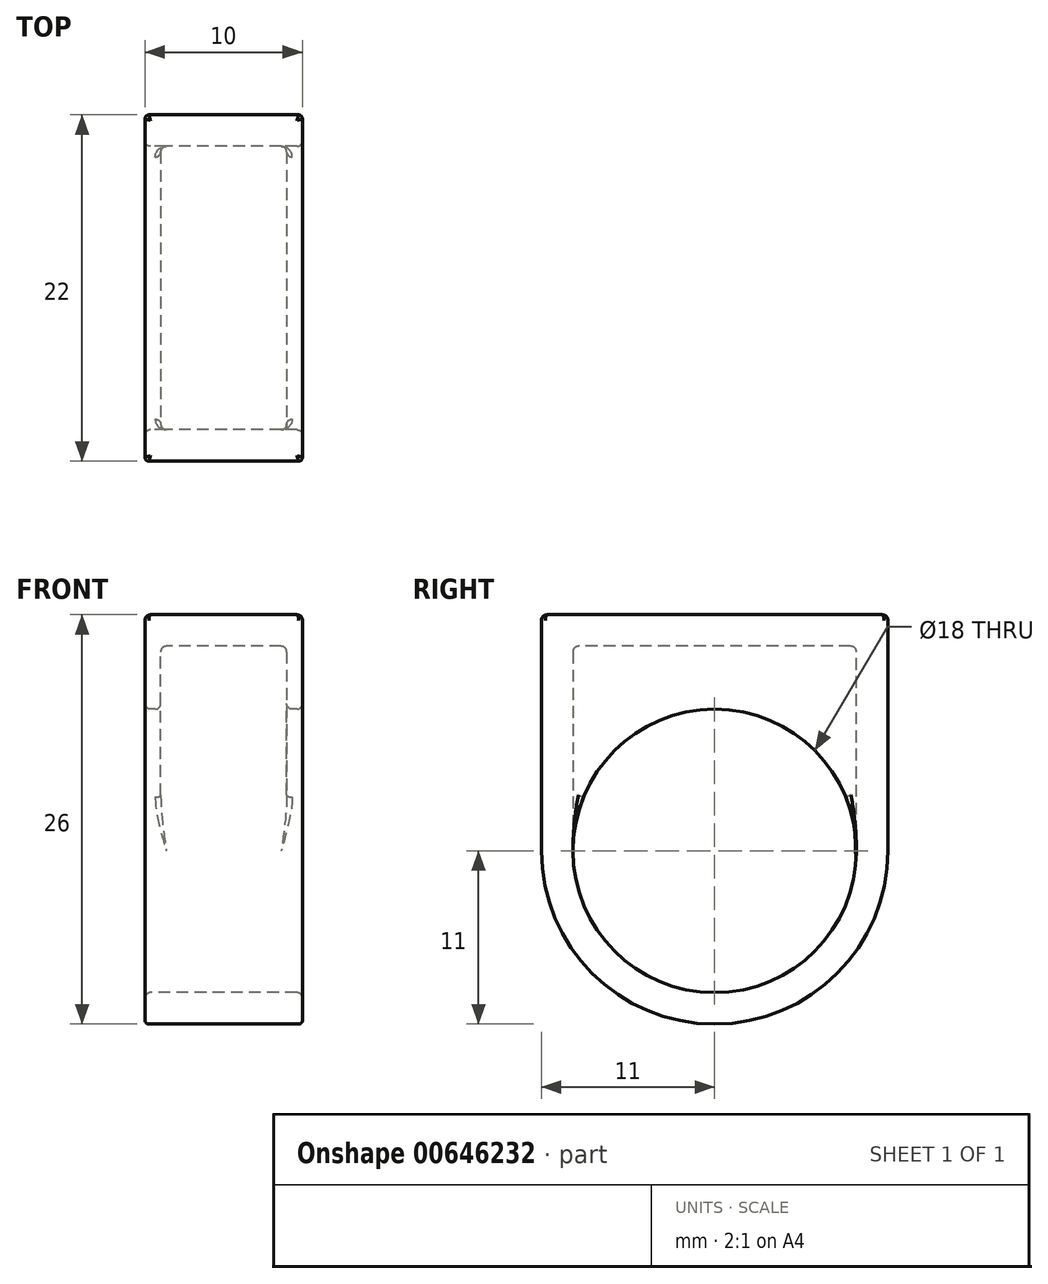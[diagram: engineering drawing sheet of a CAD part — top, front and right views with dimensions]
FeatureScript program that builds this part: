
annotation { "Feature Type Name" : "Feature", "Feature Type Description" : "" }
export const myFeature = defineFeature(function(context is Context, id is Id, definition is map)
    precondition{}
    {
        {
            var Q0;
            Q0=qCreatedBy(makeId("Right.planeOp"),FACE);
            var sketch = newSketch(context, id + "F0", { "sketchPlane" : qUnion([Q0])});
            skCircle(sketch, "E0", {"center": v(0, 0) * mm, "radius": 9 * mm});
            skArc(sketch, "E1", {"start": v(-11, 0) * mm, "mid": v(0, -11) * mm, "end": v(11, 0) * mm});
            skLineSegment(sketch, "E2", {"start": v(-11, 0) * mm, "end": v(-11, 15) * mm});
            skLineSegment(sketch, "E3", {"start": v(11, 0) * mm, "end": v(11, 15) * mm});
            skLineSegment(sketch, "E4", {"start": v(11, 15) * mm, "end": v(-11, 15) * mm});
            skSolve(sketch);
        }
        {
            var Q0;
            Q0=makeQuery(id+"F0.imprint","IMPRINT",FACE,{"disambiguationData":[TD([[makeQuery(id+"F0.imprint","IMPRINT",EDGE,{"derivedFrom":sQuery(id+"F0.wireOp",EDGE,"E0")}),-1.0]])]});
            extrude(context, id + "F1", {"entities" : qUnion([Q0]), "endBound" : BoundingType.SYMMETRIC, "depth" : 10 * mm, "offsetDistance" : 25 * mm});
        }
        {
            var Q0;
            Q0=qCreatedBy(makeId("Right.planeOp"),FACE);
            var sketch = newSketch(context, id + "F2", { "sketchPlane" : qUnion([Q0])});
            skLineSegment(sketch, "E5.0", {"start": v(9, 0) * mm, "end": v(9, 13) * mm});
            skArc(sketch, "E5.1", {"start": v(-9, 0) * mm, "mid": v(0, -9) * mm, "end": v(9, 0) * mm});
            skLineSegment(sketch, "E5.2", {"start": v(-9, 13) * mm, "end": v(-9, 0) * mm});
            skLineSegment(sketch, "E5.3", {"start": v(9, 13) * mm, "end": v(-9, 13) * mm});
            skSolve(sketch);
        }
        {
            var Q0;
            Q0 = qSketchRegion(id + "F2", true);
            extrude(context, id + "F3", {"entities" : qUnion([Q0]), "operationType" : NewBodyOperationType.REMOVE, "endBound" : BoundingType.SYMMETRIC, "depth" : 8 * mm, "offsetDistance" : 25 * mm});
        }
        {
            var Q0;
            Q0=makeQuery(id+"F1.opExtrude","CAP_EDGE",EDGE,{"disambiguationData":[OSD([sQuery(id+"F0.wireOp",EDGE,"E2")])],"isStart":true});
            var Q1;
            Q1=makeQuery(id+"F1.opExtrude","CAP_EDGE",EDGE,{"disambiguationData":[OSD([sQuery(id+"F0.wireOp",EDGE,"E2")])],"isStart":false});
            fillet(context, id + "F4", {"entities" : qUnion([Q0, Q1]), "radius" : 0.25 * mm, "tangentPropagation" : true, "allowEdgeOverflow" : false});
        }
        {
            var Q0;
            Q0=makeQuery(id+"F1.opExtrude","CAP_EDGE",EDGE,{"disambiguationData":[OSD([sQuery(id+"F0.wireOp",EDGE,"E0")])],"isStart":true});
            var Q1;
            {var subQ0=sQuery(id+"F0.wireOp",EDGE,"E2");Q1=makeQuery(id+"F4.opFillet","BLEND_FACE",FACE,{"disambiguationData":[OSD([subQ0]),TDD([makeQuery(id+"F1.opExtrude","CAP_EDGE",EDGE,{"disambiguationData":[OSD([subQ0])],"isStart":true})])]});}
            var Q2;
            Q2=makeQuery(id+"F1.opExtrude","SWEPT_EDGE",EDGE,{"disambiguationData":[OSD([sQuery(id+"F0.wireOp",EDGE,"E3"),sQuery(id+"F0.wireOp",EDGE,"E4")])]});
            var Q3;
            {var subQ0=sQuery(id+"F0.wireOp",EDGE,"E2");Q3=makeQuery(id+"F4.opFillet","BLEND_FACE",FACE,{"disambiguationData":[OSD([subQ0]),TDD([makeQuery(id+"F1.opExtrude","CAP_EDGE",EDGE,{"disambiguationData":[OSD([subQ0])],"isStart":false})])]});}
            var Q4;
            Q4=makeQuery(id+"F1.opExtrude","SWEPT_EDGE",EDGE,{"disambiguationData":[OSD([sQuery(id+"F0.wireOp",EDGE,"E2"),sQuery(id+"F0.wireOp",EDGE,"E4")])]});
            var Q5;
            {var subQ0=sQuery(id+"F0.wireOp",EDGE,"E3");Q5=makeQuery(id+"F4.opFillet","BLEND_FACE",FACE,{"disambiguationData":[OSD([subQ0]),TDD([makeQuery(id+"F1.opExtrude","CAP_EDGE",EDGE,{"disambiguationData":[OSD([subQ0])],"isStart":false})])]});}
            var Q6;
            {var subQ0=sQuery(id+"F0.wireOp",EDGE,"E1");Q6=makeQuery(id+"F4.opFillet","BLEND_FACE",FACE,{"disambiguationData":[OSD([subQ0]),TDD([makeQuery(id+"F1.opExtrude","CAP_EDGE",EDGE,{"disambiguationData":[OSD([subQ0])],"isStart":false})])]});}
            var Q7;
            Q7=makeQuery(id+"F1.opExtrude","CAP_EDGE",EDGE,{"disambiguationData":[OSD([sQuery(id+"F0.wireOp",EDGE,"E0")])],"isStart":false});
            var Q8;
            {var subQ0=sQuery(id+"F0.wireOp",EDGE,"E1");Q8=makeQuery(id+"F4.opFillet","BLEND_FACE",FACE,{"disambiguationData":[OSD([subQ0]),TDD([makeQuery(id+"F1.opExtrude","CAP_EDGE",EDGE,{"disambiguationData":[OSD([subQ0])],"isStart":true})])]});}
            var Q9;
            Q9=makeQuery(id+"F1.opExtrude","SWEPT_EDGE",EDGE,{"disambiguationData":[OSD([sQuery(id+"F0.wireOp",EDGE,"E1"),sQuery(id+"F0.wireOp",EDGE,"E2")])]});
            var Q10;
            Q10=makeQuery(id+"F3.boolean.opBoolean","INTERSECT",EDGE,{"derivedFrom":[makeQuery(id+"F1.opExtrude","SWEPT_FACE",FACE,{"disambiguationData":[OSD([sQuery(id+"F0.wireOp",EDGE,"E0")])]}),makeQuery(id+"F3.opExtrude","CAP_FACE",FACE,{"disambiguationData":[OSD([sQuery(id+"F2.wireOp",EDGE,"E5.0"),sQuery(id+"F2.wireOp",EDGE,"E5.1"),sQuery(id+"F2.wireOp",EDGE,"E5.2"),sQuery(id+"F2.wireOp",EDGE,"E5.3")])],"isStart":false})]});
            var Q11;
            Q11=makeQuery(id+"F1.opExtrude","SWEPT_FACE",FACE,{"disambiguationData":[OSD([sQuery(id+"F0.wireOp",EDGE,"E0")])]});
            var Q12;
            Q12=makeQuery(id+"F3.boolean.opBoolean","COPY",FACE,{"derivedFrom":makeQuery(id+"F3.opExtrude","CAP_FACE",FACE,{"disambiguationData":[OSD([sQuery(id+"F2.wireOp",EDGE,"E5.0"),sQuery(id+"F2.wireOp",EDGE,"E5.1"),sQuery(id+"F2.wireOp",EDGE,"E5.2"),sQuery(id+"F2.wireOp",EDGE,"E5.3")])],"isStart":false})});
            var Q13;
            Q13=makeQuery(id+"F3.boolean.opBoolean","COPY",FACE,{"derivedFrom":makeQuery(id+"F3.opExtrude","SWEPT_FACE",FACE,{"disambiguationData":[OSD([sQuery(id+"F2.wireOp",EDGE,"E5.0")])]})});
            var Q14;
            Q14=makeQuery(id+"F3.boolean.opBoolean","COPY",EDGE,{"derivedFrom":makeQuery(id+"F3.opExtrude","SWEPT_EDGE",EDGE,{"disambiguationData":[OSD([sQuery(id+"F2.wireOp",EDGE,"E5.0"),sQuery(id+"F2.wireOp",EDGE,"E5.1")])]})});
            var Q15;
            Q15=makeQuery(id+"F1.opExtrude","CAP_FACE",FACE,{"disambiguationData":[OSD([sQuery(id+"F0.wireOp",EDGE,"E0"),sQuery(id+"F0.wireOp",EDGE,"E1"),sQuery(id+"F0.wireOp",EDGE,"E2"),sQuery(id+"F0.wireOp",EDGE,"E3"),sQuery(id+"F0.wireOp",EDGE,"E4")])],"isStart":true});
            var Q16;
            {var subQ0=sQuery(id+"F0.wireOp",EDGE,"E1");Q16=makeQuery(id+"F4.opFillet","BLEND_EDGE",EDGE,{"blendedFrom":[makeQuery(id+"F1.opExtrude","CAP_EDGE",EDGE,{"disambiguationData":[OSD([subQ0])],"isStart":true}),makeQuery(id+"F1.opExtrude","SWEPT_FACE",FACE,{"disambiguationData":[OSD([subQ0])]})],"blendedInto":[makeQuery(id+"F1.opExtrude","SWEPT_FACE",FACE,{"disambiguationData":[OSD([subQ0])]})]});}
            var Q17;
            Q17=makeQuery(id+"F1.opExtrude","CAP_FACE",FACE,{"disambiguationData":[OSD([sQuery(id+"F0.wireOp",EDGE,"E0"),sQuery(id+"F0.wireOp",EDGE,"E1"),sQuery(id+"F0.wireOp",EDGE,"E2"),sQuery(id+"F0.wireOp",EDGE,"E3"),sQuery(id+"F0.wireOp",EDGE,"E4")])],"isStart":false});
            var Q18;
            Q18=makeQuery(id+"F1.opExtrude","SWEPT_FACE",FACE,{"disambiguationData":[OSD([sQuery(id+"F0.wireOp",EDGE,"E1")])]});
            var Q19;
            Q19=makeQuery(id+"F1.opExtrude","SWEPT_FACE",FACE,{"disambiguationData":[OSD([sQuery(id+"F0.wireOp",EDGE,"E2")])]});
            var Q20;
            {var subQ0=sQuery(id+"F0.wireOp",EDGE,"E1");Q20=makeQuery(id+"F4.opFillet","BLEND_EDGE",EDGE,{"blendedFrom":[makeQuery(id+"F1.opExtrude","CAP_EDGE",EDGE,{"disambiguationData":[OSD([subQ0])],"isStart":false}),makeQuery(id+"F1.opExtrude","CAP_FACE",FACE,{"disambiguationData":[OSD([sQuery(id+"F0.wireOp",EDGE,"E0"),subQ0,sQuery(id+"F0.wireOp",EDGE,"E2"),sQuery(id+"F0.wireOp",EDGE,"E3"),sQuery(id+"F0.wireOp",EDGE,"E4")])],"isStart":false})],"blendedInto":[makeQuery(id+"F1.opExtrude","CAP_FACE",FACE,{"disambiguationData":[OSD([sQuery(id+"F0.wireOp",EDGE,"E0"),subQ0,sQuery(id+"F0.wireOp",EDGE,"E2"),sQuery(id+"F0.wireOp",EDGE,"E3"),sQuery(id+"F0.wireOp",EDGE,"E4")])],"isStart":false})]});}
            var Q21;
            Q21=makeQuery(id+"F1.opExtrude","SWEPT_FACE",FACE,{"disambiguationData":[OSD([sQuery(id+"F0.wireOp",EDGE,"E3")])]});
            var Q22;
            {var subQ0=sQuery(id+"F0.wireOp",EDGE,"E1");Q22=makeQuery(id+"F4.opFillet","BLEND_EDGE",EDGE,{"blendedFrom":[makeQuery(id+"F1.opExtrude","CAP_EDGE",EDGE,{"disambiguationData":[OSD([subQ0])],"isStart":false}),makeQuery(id+"F1.opExtrude","SWEPT_FACE",FACE,{"disambiguationData":[OSD([subQ0])]})],"blendedInto":[makeQuery(id+"F1.opExtrude","SWEPT_FACE",FACE,{"disambiguationData":[OSD([subQ0])]})]});}
            var Q23;
            Q23=makeQuery(id+"F1.opExtrude","SWEPT_FACE",FACE,{"disambiguationData":[OSD([sQuery(id+"F0.wireOp",EDGE,"E4")])]});
            var Q24;
            Q24=makeQuery(id+"F4.opFillet","BLEND_EDGE",EDGE,{"blendedFrom":[makeQuery(id+"F1.opExtrude","CAP_EDGE",EDGE,{"disambiguationData":[OSD([sQuery(id+"F0.wireOp",EDGE,"E2")])],"isStart":false}),makeQuery(id+"F1.opExtrude","SWEPT_FACE",FACE,{"disambiguationData":[OSD([sQuery(id+"F0.wireOp",EDGE,"E4")])]})],"blendedInto":[makeQuery(id+"F1.opExtrude","SWEPT_FACE",FACE,{"disambiguationData":[OSD([sQuery(id+"F0.wireOp",EDGE,"E4")])]})]});
            var Q25;
            Q25=makeQuery(id+"F1.opExtrude","CAP_EDGE",EDGE,{"disambiguationData":[OSD([sQuery(id+"F0.wireOp",EDGE,"E4")])],"isStart":true});
            var Q26;
            Q26=makeQuery(id+"F1.opExtrude","CAP_EDGE",EDGE,{"disambiguationData":[OSD([sQuery(id+"F0.wireOp",EDGE,"E4")])],"isStart":false});
            var Q27;
            {var subQ0=sQuery(id+"F0.wireOp",EDGE,"E3");Q27=makeQuery(id+"F4.opFillet","BLEND_FACE",FACE,{"disambiguationData":[OSD([subQ0]),TDD([makeQuery(id+"F1.opExtrude","CAP_EDGE",EDGE,{"disambiguationData":[OSD([subQ0])],"isStart":true})])]});}
            var Q28;
            Q28=makeQuery(id+"F3.boolean.opBoolean","COPY",FACE,{"derivedFrom":makeQuery(id+"F3.opExtrude","CAP_FACE",FACE,{"disambiguationData":[OSD([sQuery(id+"F2.wireOp",EDGE,"E5.0"),sQuery(id+"F2.wireOp",EDGE,"E5.1"),sQuery(id+"F2.wireOp",EDGE,"E5.2"),sQuery(id+"F2.wireOp",EDGE,"E5.3")])],"isStart":true})});
            var Q29;
            {var subQ0=sQuery(id+"F0.wireOp",EDGE,"E1");Q29=makeQuery(id+"F4.opFillet","BLEND_EDGE",EDGE,{"blendedFrom":[makeQuery(id+"F1.opExtrude","CAP_EDGE",EDGE,{"disambiguationData":[OSD([subQ0])],"isStart":true}),makeQuery(id+"F1.opExtrude","CAP_FACE",FACE,{"disambiguationData":[OSD([sQuery(id+"F0.wireOp",EDGE,"E0"),subQ0,sQuery(id+"F0.wireOp",EDGE,"E2"),sQuery(id+"F0.wireOp",EDGE,"E3"),sQuery(id+"F0.wireOp",EDGE,"E4")])],"isStart":true})],"blendedInto":[makeQuery(id+"F1.opExtrude","CAP_FACE",FACE,{"disambiguationData":[OSD([sQuery(id+"F0.wireOp",EDGE,"E0"),subQ0,sQuery(id+"F0.wireOp",EDGE,"E2"),sQuery(id+"F0.wireOp",EDGE,"E3"),sQuery(id+"F0.wireOp",EDGE,"E4")])],"isStart":true})]});}
            var Q30;
            Q30=makeQuery(id+"F3.boolean.opBoolean","COPY",EDGE,{"derivedFrom":makeQuery(id+"F3.opExtrude","CAP_EDGE",EDGE,{"disambiguationData":[OSD([sQuery(id+"F2.wireOp",EDGE,"E5.0")])],"isStart":true})});
            var Q31;
            Q31=makeQuery(id+"F1.opExtrude","SWEPT_EDGE",EDGE,{"disambiguationData":[OSD([sQuery(id+"F0.wireOp",EDGE,"E1"),sQuery(id+"F0.wireOp",EDGE,"E3")])]});
            var Q32;
            {var subQ0=sQuery(id+"F0.wireOp",EDGE,"E2");Q32=makeQuery(id+"F4.opFillet","BLEND_EDGE",EDGE,{"blendedFrom":[makeQuery(id+"F1.opExtrude","CAP_EDGE",EDGE,{"disambiguationData":[OSD([subQ0])],"isStart":false}),makeQuery(id+"F1.opExtrude","CAP_FACE",FACE,{"disambiguationData":[OSD([sQuery(id+"F0.wireOp",EDGE,"E0"),sQuery(id+"F0.wireOp",EDGE,"E1"),subQ0,sQuery(id+"F0.wireOp",EDGE,"E3"),sQuery(id+"F0.wireOp",EDGE,"E4")])],"isStart":false})],"blendedInto":[makeQuery(id+"F1.opExtrude","CAP_FACE",FACE,{"disambiguationData":[OSD([sQuery(id+"F0.wireOp",EDGE,"E0"),sQuery(id+"F0.wireOp",EDGE,"E1"),subQ0,sQuery(id+"F0.wireOp",EDGE,"E3"),sQuery(id+"F0.wireOp",EDGE,"E4")])],"isStart":false})]});}
            var Q33;
            Q33=makeQuery(id+"F4.opFillet","BLEND_EDGE",EDGE,{"blendedFrom":[makeQuery(id+"F1.opExtrude","CAP_EDGE",EDGE,{"disambiguationData":[OSD([sQuery(id+"F0.wireOp",EDGE,"E2")])],"isStart":true}),makeQuery(id+"F1.opExtrude","SWEPT_FACE",FACE,{"disambiguationData":[OSD([sQuery(id+"F0.wireOp",EDGE,"E4")])]})],"blendedInto":[makeQuery(id+"F1.opExtrude","SWEPT_FACE",FACE,{"disambiguationData":[OSD([sQuery(id+"F0.wireOp",EDGE,"E4")])]})]});
            var Q34;
            {var subQ0=sQuery(id+"F0.wireOp",EDGE,"E2");Q34=makeQuery(id+"F4.opFillet","BLEND_EDGE",EDGE,{"blendedFrom":[makeQuery(id+"F1.opExtrude","CAP_EDGE",EDGE,{"disambiguationData":[OSD([subQ0])],"isStart":true}),makeQuery(id+"F1.opExtrude","SWEPT_FACE",FACE,{"disambiguationData":[OSD([subQ0])]})],"blendedInto":[makeQuery(id+"F1.opExtrude","SWEPT_FACE",FACE,{"disambiguationData":[OSD([subQ0])]})]});}
            var Q35;
            Q35=makeQuery(id+"F3.boolean.opBoolean","COPY",FACE,{"derivedFrom":makeQuery(id+"F3.opExtrude","SWEPT_FACE",FACE,{"disambiguationData":[OSD([sQuery(id+"F2.wireOp",EDGE,"E5.3")])]})});
            var Q36;
            Q36=makeQuery(id+"F3.boolean.opBoolean","COPY",EDGE,{"derivedFrom":makeQuery(id+"F3.opExtrude","CAP_EDGE",EDGE,{"disambiguationData":[OSD([sQuery(id+"F2.wireOp",EDGE,"E5.0")])],"isStart":false})});
            var Q37;
            Q37=makeQuery(id+"F3.boolean.opBoolean","INTERSECT",EDGE,{"derivedFrom":[makeQuery(id+"F1.opExtrude","SWEPT_FACE",FACE,{"disambiguationData":[OSD([sQuery(id+"F0.wireOp",EDGE,"E0")])]}),makeQuery(id+"F3.opExtrude","CAP_FACE",FACE,{"disambiguationData":[OSD([sQuery(id+"F2.wireOp",EDGE,"E5.0"),sQuery(id+"F2.wireOp",EDGE,"E5.1"),sQuery(id+"F2.wireOp",EDGE,"E5.2"),sQuery(id+"F2.wireOp",EDGE,"E5.3")])],"isStart":true})]});
            var Q38;
            Q38=makeQuery(id+"F3.boolean.opBoolean","COPY",EDGE,{"derivedFrom":makeQuery(id+"F3.opExtrude","CAP_EDGE",EDGE,{"disambiguationData":[OSD([sQuery(id+"F2.wireOp",EDGE,"E5.3")])],"isStart":true})});
            var Q39;
            Q39=makeQuery(id+"F3.boolean.opBoolean","COPY",EDGE,{"derivedFrom":makeQuery(id+"F3.opExtrude","CAP_EDGE",EDGE,{"disambiguationData":[OSD([sQuery(id+"F2.wireOp",EDGE,"E5.3")])],"isStart":false})});
            var Q40;
            Q40=makeQuery(id+"F3.boolean.opBoolean","COPY",FACE,{"derivedFrom":makeQuery(id+"F3.opExtrude","SWEPT_FACE",FACE,{"disambiguationData":[OSD([sQuery(id+"F2.wireOp",EDGE,"E5.2")])]})});
            var Q41;
            Q41=makeQuery(id+"F3.boolean.opBoolean","COPY",EDGE,{"derivedFrom":makeQuery(id+"F3.opExtrude","SWEPT_EDGE",EDGE,{"disambiguationData":[OSD([sQuery(id+"F2.wireOp",EDGE,"E5.2"),sQuery(id+"F2.wireOp",EDGE,"E5.3")])]})});
            var Q42;
            Q42=makeQuery(id+"F3.boolean.opBoolean","COPY",EDGE,{"derivedFrom":makeQuery(id+"F3.opExtrude","SWEPT_EDGE",EDGE,{"disambiguationData":[OSD([sQuery(id+"F2.wireOp",EDGE,"E5.1"),sQuery(id+"F2.wireOp",EDGE,"E5.2")])]})});
            var Q43;
            Q43=makeQuery(id+"F3.boolean.opBoolean","COPY",EDGE,{"derivedFrom":makeQuery(id+"F3.opExtrude","SWEPT_EDGE",EDGE,{"disambiguationData":[OSD([sQuery(id+"F2.wireOp",EDGE,"E5.0"),sQuery(id+"F2.wireOp",EDGE,"E5.3")])]})});
            var Q44;
            Q44=makeQuery(id+"F4.opFillet","BLEND_EDGE",EDGE,{"blendedFrom":[makeQuery(id+"F1.opExtrude","CAP_EDGE",EDGE,{"disambiguationData":[OSD([sQuery(id+"F0.wireOp",EDGE,"E1")])],"isStart":false}),makeQuery(id+"F1.opExtrude","CAP_EDGE",EDGE,{"disambiguationData":[OSD([sQuery(id+"F0.wireOp",EDGE,"E2")])],"isStart":false})],"blendedInto":[]});
            var Q45;
            Q45=makeQuery(id+"F4.opFillet","BLEND_EDGE",EDGE,{"blendedFrom":[makeQuery(id+"F1.opExtrude","CAP_EDGE",EDGE,{"disambiguationData":[OSD([sQuery(id+"F0.wireOp",EDGE,"E1")])],"isStart":false}),makeQuery(id+"F1.opExtrude","CAP_EDGE",EDGE,{"disambiguationData":[OSD([sQuery(id+"F0.wireOp",EDGE,"E3")])],"isStart":false})],"blendedInto":[]});
            var Q46;
            {var subQ0=sQuery(id+"F0.wireOp",EDGE,"E2");Q46=makeQuery(id+"F4.opFillet","BLEND_EDGE",EDGE,{"blendedFrom":[makeQuery(id+"F1.opExtrude","CAP_EDGE",EDGE,{"disambiguationData":[OSD([subQ0])],"isStart":false}),makeQuery(id+"F1.opExtrude","SWEPT_FACE",FACE,{"disambiguationData":[OSD([subQ0])]})],"blendedInto":[makeQuery(id+"F1.opExtrude","SWEPT_FACE",FACE,{"disambiguationData":[OSD([subQ0])]})]});}
            var Q47;
            {var subQ0=sQuery(id+"F0.wireOp",EDGE,"E3");Q47=makeQuery(id+"F4.opFillet","BLEND_EDGE",EDGE,{"blendedFrom":[makeQuery(id+"F1.opExtrude","CAP_EDGE",EDGE,{"disambiguationData":[OSD([subQ0])],"isStart":true}),makeQuery(id+"F1.opExtrude","CAP_FACE",FACE,{"disambiguationData":[OSD([sQuery(id+"F0.wireOp",EDGE,"E0"),sQuery(id+"F0.wireOp",EDGE,"E1"),sQuery(id+"F0.wireOp",EDGE,"E2"),subQ0,sQuery(id+"F0.wireOp",EDGE,"E4")])],"isStart":true})],"blendedInto":[makeQuery(id+"F1.opExtrude","CAP_FACE",FACE,{"disambiguationData":[OSD([sQuery(id+"F0.wireOp",EDGE,"E0"),sQuery(id+"F0.wireOp",EDGE,"E1"),sQuery(id+"F0.wireOp",EDGE,"E2"),subQ0,sQuery(id+"F0.wireOp",EDGE,"E4")])],"isStart":true})]});}
            var Q48;
            {var subQ0=sQuery(id+"F0.wireOp",EDGE,"E3");Q48=makeQuery(id+"F4.opFillet","BLEND_EDGE",EDGE,{"blendedFrom":[makeQuery(id+"F1.opExtrude","CAP_EDGE",EDGE,{"disambiguationData":[OSD([subQ0])],"isStart":false}),makeQuery(id+"F1.opExtrude","CAP_FACE",FACE,{"disambiguationData":[OSD([sQuery(id+"F0.wireOp",EDGE,"E0"),sQuery(id+"F0.wireOp",EDGE,"E1"),sQuery(id+"F0.wireOp",EDGE,"E2"),subQ0,sQuery(id+"F0.wireOp",EDGE,"E4")])],"isStart":false})],"blendedInto":[makeQuery(id+"F1.opExtrude","CAP_FACE",FACE,{"disambiguationData":[OSD([sQuery(id+"F0.wireOp",EDGE,"E0"),sQuery(id+"F0.wireOp",EDGE,"E1"),sQuery(id+"F0.wireOp",EDGE,"E2"),subQ0,sQuery(id+"F0.wireOp",EDGE,"E4")])],"isStart":false})]});}
            var Q49;
            Q49=makeQuery(id+"F4.opFillet","BLEND_EDGE",EDGE,{"blendedFrom":[makeQuery(id+"F1.opExtrude","CAP_EDGE",EDGE,{"disambiguationData":[OSD([sQuery(id+"F0.wireOp",EDGE,"E1")])],"isStart":true}),makeQuery(id+"F1.opExtrude","CAP_EDGE",EDGE,{"disambiguationData":[OSD([sQuery(id+"F0.wireOp",EDGE,"E3")])],"isStart":true})],"blendedInto":[]});
            var Q50;
            Q50=makeQuery(id+"F4.opFillet","BLEND_EDGE",EDGE,{"blendedFrom":[makeQuery(id+"F1.opExtrude","CAP_EDGE",EDGE,{"disambiguationData":[OSD([sQuery(id+"F0.wireOp",EDGE,"E1")])],"isStart":true}),makeQuery(id+"F1.opExtrude","CAP_EDGE",EDGE,{"disambiguationData":[OSD([sQuery(id+"F0.wireOp",EDGE,"E2")])],"isStart":true})],"blendedInto":[]});
            var Q51;
            Q51=makeQuery(id+"F3.boolean.opBoolean","COPY",EDGE,{"derivedFrom":makeQuery(id+"F3.opExtrude","CAP_EDGE",EDGE,{"disambiguationData":[OSD([sQuery(id+"F2.wireOp",EDGE,"E5.2")])],"isStart":true})});
            var Q52;
            Q52=makeQuery(id+"F3.boolean.opBoolean","COPY",EDGE,{"derivedFrom":makeQuery(id+"F3.opExtrude","CAP_EDGE",EDGE,{"disambiguationData":[OSD([sQuery(id+"F2.wireOp",EDGE,"E5.2")])],"isStart":false})});
            var Q53;
            {var subQ0=sQuery(id+"F0.wireOp",EDGE,"E2");Q53=makeQuery(id+"F4.opFillet","BLEND_EDGE",EDGE,{"blendedFrom":[makeQuery(id+"F1.opExtrude","CAP_EDGE",EDGE,{"disambiguationData":[OSD([subQ0])],"isStart":true}),makeQuery(id+"F1.opExtrude","CAP_FACE",FACE,{"disambiguationData":[OSD([sQuery(id+"F0.wireOp",EDGE,"E0"),sQuery(id+"F0.wireOp",EDGE,"E1"),subQ0,sQuery(id+"F0.wireOp",EDGE,"E3"),sQuery(id+"F0.wireOp",EDGE,"E4")])],"isStart":true})],"blendedInto":[makeQuery(id+"F1.opExtrude","CAP_FACE",FACE,{"disambiguationData":[OSD([sQuery(id+"F0.wireOp",EDGE,"E0"),sQuery(id+"F0.wireOp",EDGE,"E1"),subQ0,sQuery(id+"F0.wireOp",EDGE,"E3"),sQuery(id+"F0.wireOp",EDGE,"E4")])],"isStart":true})]});}
            var Q54;
            {var subQ0=sQuery(id+"F0.wireOp",EDGE,"E3");Q54=makeQuery(id+"F4.opFillet","BLEND_EDGE",EDGE,{"blendedFrom":[makeQuery(id+"F1.opExtrude","CAP_EDGE",EDGE,{"disambiguationData":[OSD([subQ0])],"isStart":true}),makeQuery(id+"F1.opExtrude","SWEPT_FACE",FACE,{"disambiguationData":[OSD([subQ0])]})],"blendedInto":[makeQuery(id+"F1.opExtrude","SWEPT_FACE",FACE,{"disambiguationData":[OSD([subQ0])]})]});}
            var Q55;
            Q55=makeQuery(id+"F4.opFillet","BLEND_EDGE",EDGE,{"blendedFrom":[makeQuery(id+"F1.opExtrude","CAP_EDGE",EDGE,{"disambiguationData":[OSD([sQuery(id+"F0.wireOp",EDGE,"E3")])],"isStart":true}),makeQuery(id+"F1.opExtrude","SWEPT_FACE",FACE,{"disambiguationData":[OSD([sQuery(id+"F0.wireOp",EDGE,"E4")])]})],"blendedInto":[makeQuery(id+"F1.opExtrude","SWEPT_FACE",FACE,{"disambiguationData":[OSD([sQuery(id+"F0.wireOp",EDGE,"E4")])]})]});
            var Q56;
            {var subQ0=sQuery(id+"F0.wireOp",EDGE,"E3");Q56=makeQuery(id+"F4.opFillet","BLEND_EDGE",EDGE,{"blendedFrom":[makeQuery(id+"F1.opExtrude","CAP_EDGE",EDGE,{"disambiguationData":[OSD([subQ0])],"isStart":false}),makeQuery(id+"F1.opExtrude","SWEPT_FACE",FACE,{"disambiguationData":[OSD([subQ0])]})],"blendedInto":[makeQuery(id+"F1.opExtrude","SWEPT_FACE",FACE,{"disambiguationData":[OSD([subQ0])]})]});}
            var Q57;
            Q57=makeQuery(id+"F4.opFillet","BLEND_EDGE",EDGE,{"blendedFrom":[makeQuery(id+"F1.opExtrude","CAP_EDGE",EDGE,{"disambiguationData":[OSD([sQuery(id+"F0.wireOp",EDGE,"E3")])],"isStart":false}),makeQuery(id+"F1.opExtrude","SWEPT_FACE",FACE,{"disambiguationData":[OSD([sQuery(id+"F0.wireOp",EDGE,"E4")])]})],"blendedInto":[makeQuery(id+"F1.opExtrude","SWEPT_FACE",FACE,{"disambiguationData":[OSD([sQuery(id+"F0.wireOp",EDGE,"E4")])]})]});
            fillet(context, id + "F5", {"entities" : qUnion([Q0, Q1, Q2, Q3, Q4, Q5, Q6, Q7, Q8, Q9, Q10, Q11, Q12, Q13, Q14, Q15, Q16, Q17, Q18, Q19, Q20, Q21, Q22, Q23, Q24, Q25, Q26, Q27, Q28, Q29, Q30, Q31, Q32, Q33, Q34, Q35, Q36, Q37, Q38, Q39, Q40, Q41, Q42, Q43, Q44, Q45, Q46, Q47, Q48, Q49, Q50, Q51, Q52, Q53, Q54, Q55, Q56, Q57]), "radius" : 0.35 * mm, "tangentPropagation" : true, "allowEdgeOverflow" : false});
        }
    });
